# Revit family: Double Hung with Trim
name_source: partatom
category: Windows
revit_build: Autodesk Revit Architecture 2012 (Build: 20110210_1515)
units: mm (PartAtom-declared; Revit-internal decimal feet)

## types (9) — shared parameters
Assembly Code = B2020100
Glass Pane Material = Glass
Sash Material = Sash
Trim Exterior Material = Trim
Trim Interior Material = Trim
Trim Projection - Ext. = 0' - 0 1/2"
Trim Projection - Int. = 0' - 0 3/4"
Trim Width - Exterior = 0' - 3 1/2"
Trim Width - Interior = 0' - 3 1/2"
Wall Closure = By host
Window Inset = 0' - 0 3/4"

## per-type parameters (varying)
| type | Default Sill Height | Height | Width |
| 36" x 48" | 3' - 0" | 4' - 0" | 3' - 0" |
| 24" x 48" | 3' - 0" | 4' - 0" | 2' - 0" |
| 24" x 24" | 3' - 0" | 2' - 0" | 2' - 0" |
| 16" x 24" | 3' - 0" | 2' - 0" | 1' - 4" |
| 16" x 48" | 3' - 0" | 4' - 0" | 1' - 4" |
| 16" x 72" | 1' - 0" | 6' - 0" | 1' - 4" |
| 24" x 72" | 1' - 0" | 6' - 0" | 2' - 0" |
| 36" x 24" | 3' - 0" | 2' - 0" | 3' - 0" |
| 36" x 72" | 1' - 0" | 6' - 0" | 3' - 0" |
